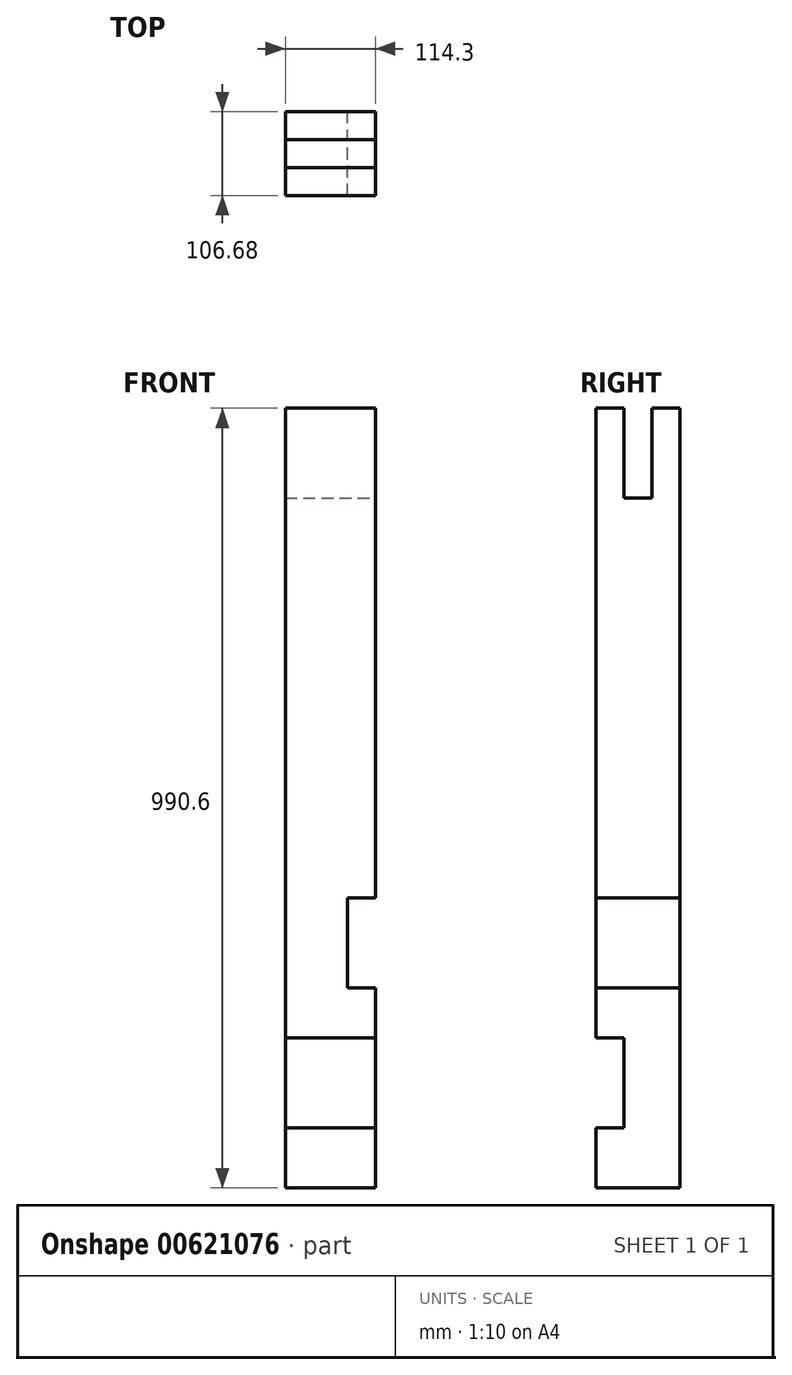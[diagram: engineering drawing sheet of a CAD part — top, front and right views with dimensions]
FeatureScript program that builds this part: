
annotation { "Feature Type Name" : "Feature", "Feature Type Description" : "" }
export const myFeature = defineFeature(function(context is Context, id is Id, definition is map)
    precondition{}
    {
        {
            var Q0;
            Q0=qCreatedBy(makeId("Top.planeOp"),FACE);
            var sketch = newSketch(context, id + "F0", { "sketchPlane" : qUnion([Q0])});
            skLineSegment(sketch, "E0.bottom", {"start": v(-57.15, 53.34) * mm, "end": v(57.15, 53.34) * mm});
            skLineSegment(sketch, "E0.top", {"start": v(-57.15, -53.34) * mm, "end": v(57.15, -53.34) * mm});
            skLineSegment(sketch, "E0.left", {"start": v(-57.15, 53.34) * mm, "end": v(-57.15, -53.34) * mm});
            skLineSegment(sketch, "E0.right", {"start": v(57.15, 53.34) * mm, "end": v(57.15, -53.34) * mm});
            skSolve(sketch);
        }
        {
            var Q0;
            Q0=makeQuery(id+"F0.imprint","IMPRINT",FACE,{"disambiguationData":[TD([[makeQuery(id+"F0.imprint","IMPRINT",EDGE,{"derivedFrom":sQuery(id+"F0.wireOp",EDGE,"E0.bottom")}),-1.0]])]});
            extrude(context, id + "F1", {"entities" : qUnion([Q0]), "depth" : 990.6 * mm, "offsetDistance" : 25.4 * mm});
        }
        {
            var Q0;
            Q0=makeQuery(id+"F1.opExtrude","CAP_FACE",FACE,{"disambiguationData":[OSD([sQuery(id+"F0.wireOp",EDGE,"E0.bottom"),sQuery(id+"F0.wireOp",EDGE,"E0.top"),sQuery(id+"F0.wireOp",EDGE,"E0.left"),sQuery(id+"F0.wireOp",EDGE,"E0.right")])],"isStart":false});
            var sketch = newSketch(context, id + "F2", { "sketchPlane" : qUnion([Q0])});
            skLineSegment(sketch, "E1.bottom", {"start": v(-57.15, 17.78) * mm, "end": v(57.15, 17.78) * mm});
            skLineSegment(sketch, "E1.top", {"start": v(-57.15, -17.78) * mm, "end": v(57.15, -17.78) * mm});
            skLineSegment(sketch, "E1.left", {"start": v(-57.15, 17.78) * mm, "end": v(-57.15, -17.78) * mm});
            skLineSegment(sketch, "E1.right", {"start": v(57.15, 17.78) * mm, "end": v(57.15, -17.78) * mm});
            skSolve(sketch);
        }
        {
            var Q0;
            Q0 = qSketchRegion(id + "F2", true);
            extrude(context, id + "F3", {"entities" : qUnion([Q0]), "operationType" : NewBodyOperationType.REMOVE, "oppositeDirection" : true, "depth" : 114.3 * mm, "offsetDistance" : 25.4 * mm});
        }
        {
            var Q0;
            Q0=makeQuery(id+"F1.opExtrude","SWEPT_FACE",FACE,{"disambiguationData":[OSD([sQuery(id+"F0.wireOp",EDGE,"E0.top")])]});
            var sketch = newSketch(context, id + "F4", { "sketchPlane" : qUnion([Q0])});
            skLineSegment(sketch, "E2.bottom", {"start": v(-57.15, 190.5) * mm, "end": v(57.15, 190.5) * mm});
            skLineSegment(sketch, "E2.top", {"start": v(-57.15, 76.2) * mm, "end": v(57.15, 76.2) * mm});
            skLineSegment(sketch, "E2.left", {"start": v(-57.15, 190.5) * mm, "end": v(-57.15, 76.2) * mm});
            skLineSegment(sketch, "E2.right", {"start": v(57.15, 190.5) * mm, "end": v(57.15, 76.2) * mm});
            skSolve(sketch);
        }
        {
            var Q0;
            Q0 = qSketchRegion(id + "F4", true);
            extrude(context, id + "F5", {"entities" : qUnion([Q0]), "operationType" : NewBodyOperationType.REMOVE, "oppositeDirection" : true, "depth" : 35.56 * mm, "offsetDistance" : 25.4 * mm});
        }
        {
            var Q0;
            Q0=makeQuery(id+"F1.opExtrude","SWEPT_FACE",FACE,{"disambiguationData":[OSD([sQuery(id+"F0.wireOp",EDGE,"E0.right")])]});
            var sketch = newSketch(context, id + "F6", { "sketchPlane" : qUnion([Q0])});
            skLineSegment(sketch, "E3.bottom", {"start": v(-53.34, 368.3) * mm, "end": v(53.34, 368.3) * mm});
            skLineSegment(sketch, "E3.top", {"start": v(-53.34, 254) * mm, "end": v(53.34, 254) * mm});
            skLineSegment(sketch, "E3.left", {"start": v(-53.34, 368.3) * mm, "end": v(-53.34, 254) * mm});
            skLineSegment(sketch, "E3.right", {"start": v(53.34, 368.3) * mm, "end": v(53.34, 254) * mm});
            skSolve(sketch);
        }
        {
            var Q0;
            Q0=makeQuery(id+"F6.imprint","IMPRINT",FACE,{"disambiguationData":[TD([[makeQuery(id+"F6.imprint","IMPRINT",EDGE,{"derivedFrom":sQuery(id+"F6.wireOp",EDGE,"E3.bottom")}),-1.0]])]});
            extrude(context, id + "F7", {"entities" : qUnion([Q0]), "operationType" : NewBodyOperationType.REMOVE, "oppositeDirection" : true, "depth" : 35.56 * mm, "offsetDistance" : 25.4 * mm});
        }
    });
